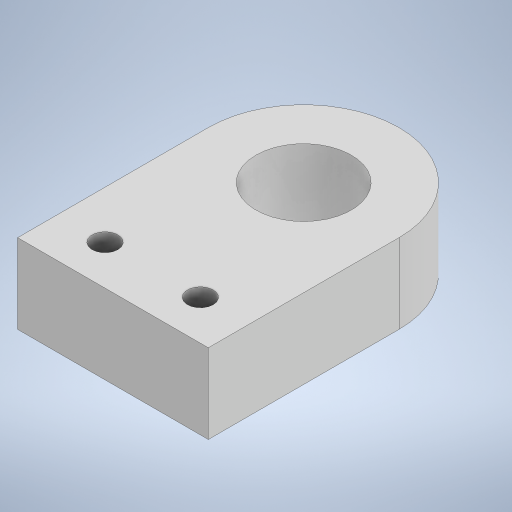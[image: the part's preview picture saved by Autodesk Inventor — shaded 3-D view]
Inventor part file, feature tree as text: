
AUTODESK INVENTOR PART (.ipt)
format: ipt  version: 2023.2 (Build 272271030, 271C)  size: 238,080 bytes
history: native  units: mm
features: extrude x3, sketch x3, projected_geometry x2
ambient origin geometry x8: Origin, YZ Plane, XZ Plane, XY Plane, X Axis, Y Axis, Z Axis, Center Point
bodies: Solid1 (feature_tree)
feature tree (8):
  extrude  "Extrusion1"  Depth=60.0mm
  extrude  "Extrusion2"  Depth=25.0mm TaperAngle=0.0deg
  extrude  "Extrusion3"  Depth=3.0mm
  sketch  "Sketch1"  dims[d0=60.0mm d1=60.0mm]
  sketch  "Sketch2"  dims[d2=30.0mm d3=25.0mm d4=0.0mm]
  projected_geometry  "Projected Loop1"
  sketch  "Sketch3"  dims[d5=65.0mm d6=8.1mm d7=30.0mm d8=0.0mm d9=0.0mm d10=13.1mm d11=13.1mm d12=3.0mm d13=0.0mm]
  projected_geometry  "Projected Loop2"
